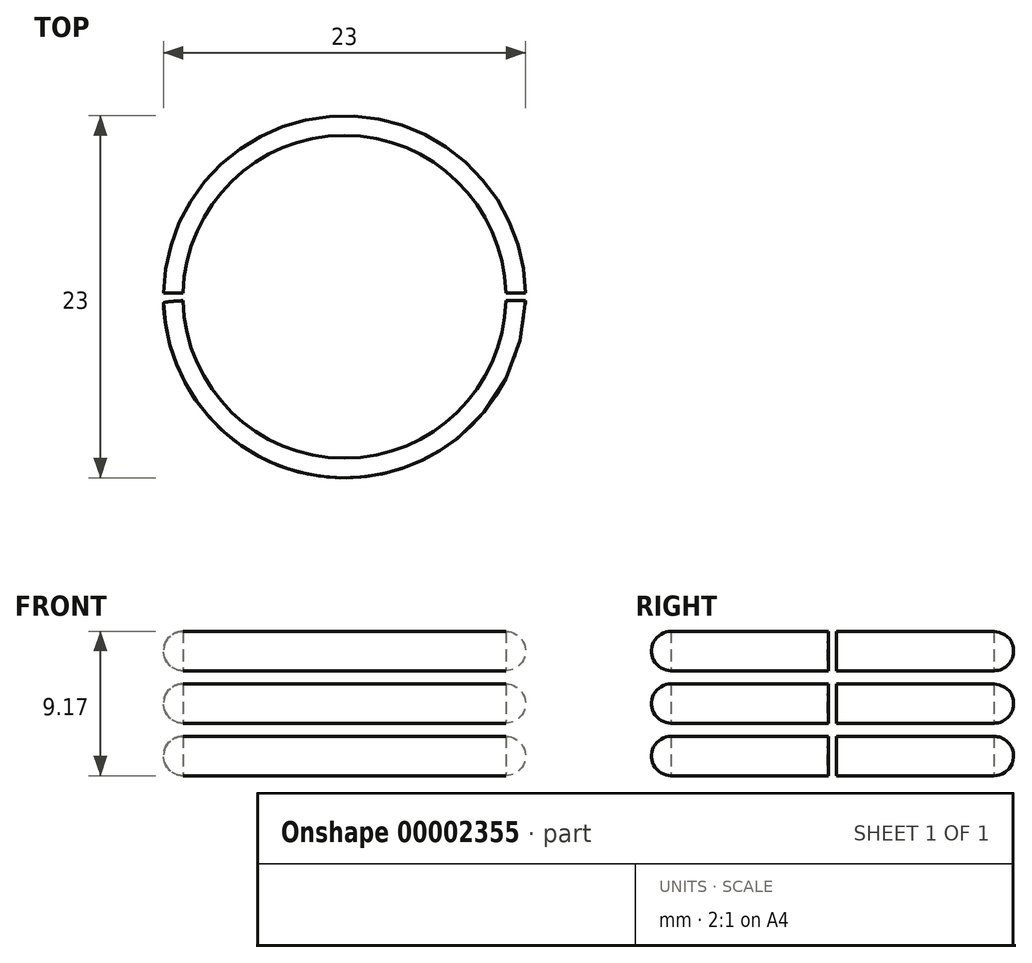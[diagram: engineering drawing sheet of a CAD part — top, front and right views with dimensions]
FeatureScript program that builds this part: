
annotation { "Feature Type Name" : "Feature", "Feature Type Description" : "" }
export const myFeature = defineFeature(function(context is Context, id is Id, definition is map)
    precondition{}
    {
        {
            var Q0;
            Q0=qCreatedBy(makeId("Top.planeOp"),FACE);
            var sketch = newSketch(context, id + "F0", { "sketchPlane" : qUnion([Q0])});
            skCircle(sketch, "E0", {"center": v(0, 0) * mm, "radius": 17.5 * mm});
            skSolve(sketch);
        }
        {
            var Q0;
            Q0=qSketchRegion(id+"F0",true);
            extrude(context, id + "F1", {"entities" : qUnion([Q0]), "depth" : 6 * mm, "hasSecondDirection" : true, "secondDirectionOppositeDirection" : true, "secondDirectionDepth" : 9 * mm});
        }
        {
            var Q0;
            Q0=makeQuery(id+"F1.opExtrude","CAP_FACE",FACE,{"disambiguationData":[OSD([sQuery(id+"F0.wireOp",EDGE,"E0")])],"isStart":false});
            var sketch = newSketch(context, id + "F2", { "sketchPlane" : qUnion([Q0])});
            skCircle(sketch, "E1", {"center": v(0, 0) * mm, "radius": 10.25 * mm});
            skSolve(sketch);
        }
        {
            var Q0;
            Q0=qSketchRegion(id+"F2",true);
            extrude(context, id + "F3", {"entities" : qUnion([Q0]), "operationType" : NewBodyOperationType.ADD, "depth" : 10 * mm});
        }
        {
            var Q0;
            Q0=qCreatedBy(makeId("Top.planeOp"),FACE);
            var sketch = newSketch(context, id + "F4", { "sketchPlane" : qUnion([Q0])});
            skLineSegment(sketch, "E2", {"start": v(0, 0) * mm, "end": v(0, 17.5) * mm, "construction": true});
            skLineSegment(sketch, "E3", {"start": v(0, 18.5) * mm, "end": v(2, 18.4) * mm});
            skLineSegment(sketch, "E4", {"start": v(2, 18.4) * mm, "end": v(1.89, 17.4) * mm});
            skArc(sketch, "E5.0", {"start": v(1.89, 17.4) * mm, "mid": v(0.95, 17.47) * mm, "end": v(0, 17.5) * mm});
            skLineSegment(sketch, "E6", {"start": v(0, 17.5) * mm, "end": v(0, 18.5) * mm});
            skLineSegment(sketch, "E7", {"start": v(1.89, 17.4) * mm, "end": v(0, 0) * mm, "construction": true});
            skSolve(sketch);
        }
        {
            var Q0;
            Q0=qSketchRegion(id+"F4",true);
            var Q1;
            Q1=makeQuery(id+"F1.opExtrude","CAP_FACE",FACE,{"disambiguationData":[OSD([sQuery(id+"F0.wireOp",EDGE,"E0")])],"isStart":false});
            var Q3;
            Q3=makeQuery(id+"F1.opExtrude","CAP_FACE",FACE,{"disambiguationData":[OSD([sQuery(id+"F0.wireOp",EDGE,"E0")])],"isStart":true});
            extrude(context, id + "F5", {"entities" : qUnion([Q0]), "operationType" : NewBodyOperationType.ADD, "endBound" : BoundingType.UP_TO_SURFACE, "endBoundEntityFace" : qUnion([Q1]), "depth" : 6 * mm, "hasSecondDirection" : true, "secondDirectionBound" : SecondDirectionBoundingType.UP_TO_SURFACE, "secondDirectionOppositeDirection" : true, "secondDirectionBoundEntityFace" : qUnion([Q3]), "secondDirectionDepth" : 9 * mm});
        }
        {
            var Q0;
            Q0=makeQuery(id+"F5.opExtrude","SWEPT_FACE",FACE,{"disambiguationData":[OSD([sQuery(id+"F4.wireOp",EDGE,"E3")])]});
            var Q1;
            Q1=makeQuery(id+"F5.opExtrude","SWEPT_FACE",FACE,{"disambiguationData":[OSD([sQuery(id+"F4.wireOp",EDGE,"E4")])]});
            var Q2;
            Q2=makeQuery(id+"F5.opExtrude","SWEPT_FACE",FACE,{"disambiguationData":[OSD([sQuery(id+"F4.wireOp",EDGE,"E6")])]});
            var Q3;
            Q3=makeQuery(id+"F1.opExtrude","CAP_EDGE",EDGE,{"disambiguationData":[OSD([sQuery(id+"F0.wireOp",EDGE,"E0")])],"isStart":false});
            circularPattern(context, id + "F6", {"faces" : qUnion([Q0, Q1, Q2]), "axis" : qUnion([Q3]), "angle" : 360 * degree, "instanceCount" : 30, "equalSpace" : true, "patternType" : PatternType.FACE});
        }
        {
            var Q0;
            Q0=qCreatedBy(makeId("Front.planeOp"),FACE);
            var sketch = newSketch(context, id + "F7", { "sketchPlane" : qUnion([Q0])});
            skArc(sketch, "E8", {"start": v(-10.25, 16) * mm, "mid": v(-11.5, 14.75) * mm, "end": v(-10.25, 13.5) * mm});
            skArc(sketch, "E9", {"start": v(-10.25, 12.67) * mm, "mid": v(-11.5, 11.42) * mm, "end": v(-10.25, 10.17) * mm});
            skLineSegment(sketch, "E10", {"start": v(-10.25, 16) * mm, "end": v(-10.25, 13.5) * mm});
            skArc(sketch, "E11", {"start": v(-10.25, 9.33) * mm, "mid": v(-11.5, 8.08) * mm, "end": v(-10.25, 6.83) * mm});
            skLineSegment(sketch, "E12", {"start": v(-10.25, 13.5) * mm, "end": v(-10.25, 12.67) * mm, "construction": true});
            skLineSegment(sketch, "E13", {"start": v(-10.25, 12.67) * mm, "end": v(-10.25, 10.17) * mm});
            skLineSegment(sketch, "E14", {"start": v(-10.25, 10.17) * mm, "end": v(-10.25, 9.33) * mm, "construction": true});
            skLineSegment(sketch, "E15", {"start": v(-10.25, 9.33) * mm, "end": v(-10.25, 6.83) * mm});
            skLineSegment(sketch, "E16", {"start": v(-10.25, 6.83) * mm, "end": v(-10.25, 6) * mm, "construction": true});
            skSolve(sketch);
        }
        {
            var Q0;
            Q0=makeQuery(id+"F7.imprint","IMPRINT",FACE,{"disambiguationData":[TD([[makeQuery(id+"F7.imprint","IMPRINT",EDGE,{"derivedFrom":sQuery(id+"F7.wireOp",EDGE,"E8")}),1.0]])]});
            var Q1;
            Q1=makeQuery(id+"F7.imprint","IMPRINT",FACE,{"disambiguationData":[TD([[makeQuery(id+"F7.imprint","IMPRINT",EDGE,{"derivedFrom":sQuery(id+"F7.wireOp",EDGE,"E9")}),1.0]])]});
            var Q2;
            Q2=makeQuery(id+"F7.imprint","IMPRINT",FACE,{"disambiguationData":[TD([[makeQuery(id+"F7.imprint","IMPRINT",EDGE,{"derivedFrom":sQuery(id+"F7.wireOp",EDGE,"E11")}),1.0]])]});
            var Q3;
            Q3=sQuery(id+"F7.wireOp",EDGE,"E8");
            var Q4;
            Q4=sQuery(id+"F7.wireOp",EDGE,"E9");
            var Q5;
            Q5=sQuery(id+"F7.wireOp",EDGE,"E11");
            var Q6;
            Q6=makeQuery(id+"F3.opExtrude","CAP_EDGE",EDGE,{"disambiguationData":[OSD([sQuery(id+"F2.wireOp",EDGE,"E1")])],"isStart":false});
            revolve(context, id + "F8", {"entities" : qUnion([Q0, Q1, Q2]), "surfaceEntities" : qUnion([Q3, Q4, Q5]), "axis" : qUnion([Q6]), "revolveType" : RevolveType.FULL});
        }
        {
            var Q0;
            Q0=makeQuery(id+"F3.opExtrude","CAP_FACE",FACE,{"disambiguationData":[OSD([sQuery(id+"F2.wireOp",EDGE,"E1")])],"isStart":false});
            var sketch = newSketch(context, id + "F9", { "sketchPlane" : qUnion([Q0])});
            skCircle(sketch, "E17", {"center": v(0, 0) * mm, "radius": 8.25 * mm});
            skSolve(sketch);
        }
        {
            var Q0;
            Q0 = qSketchRegion(id + "F9", true);
            var Q1;
            Q1=makeQuery(id+"F5.boolean.opBoolean","MERGE",FACE,{"derivedFrom":[makeQuery(id+"F1.opExtrude","CAP_FACE",FACE,{"disambiguationData":[OSD([sQuery(id+"F0.wireOp",EDGE,"E0")])],"isStart":false}),makeQuery(id+"F5.opExtrude","CAP_FACE",FACE,{"disambiguationData":[OSD([sQuery(id+"F4.wireOp",EDGE,"E3"),sQuery(id+"F4.wireOp",EDGE,"E4"),sQuery(id+"F4.wireOp",EDGE,"E5.0"),sQuery(id+"F4.wireOp",EDGE,"E6")])],"isStart":false})]});
            extrude(context, id + "F10", {"entities" : qUnion([Q0]), "operationType" : NewBodyOperationType.REMOVE, "endBound" : BoundingType.UP_TO_SURFACE, "oppositeDirection" : true, "endBoundEntityFace" : qUnion([Q1]), "depth" : 25 * mm});
        }
        {
            var Q0;
            {var subQ0=sQuery(id+"F9.wireOp",EDGE,"E17");Q0=makeQuery(id+"F14.boolean.opBoolean","SPLIT",FACE,{"disambiguationData":[TD([makeQuery(id+"F14.opExtrude","SWEPT_FACE",FACE,{"disambiguationData":[OSD([sQuery(id+"F13.wireOp",EDGE,"E19.rect.bottom")])]})])],"derivedFrom":makeQuery(id+"F10.boolean.opBoolean","COPY",FACE,{"derivedFrom":makeQuery(id+"F10.opExtrude","CAP_FACE",FACE,{"disambiguationData":[OSD([subQ0])],"isStart":false})})});}
            var sketch = newSketch(context, id + "F11", { "sketchPlane" : qUnion([Q0])});
            skCircle(sketch, "E18", {"center": v(0, 0) * mm, "radius": 3 * mm});
            skSolve(sketch);
        }
        {
            var Q0;
            Q0 = qSketchRegion(id + "F11", true);
            extrude(context, id + "F12", {"entities" : qUnion([Q0]), "operationType" : NewBodyOperationType.REMOVE, "endBound" : BoundingType.THROUGH_ALL, "oppositeDirection" : true, "depth" : 25 * mm});
        }
        {
            var Q0;
            Q0=makeQuery(id+"F9.imprint","IMPRINT",FACE,{"disambiguationData":[TD([[makeQuery(id+"F9.imprint","IMPRINT",EDGE,{"derivedFrom":sQuery(id+"F9.wireOp",EDGE,"E17")}),-1.0]])]});
            var sketch = newSketch(context, id + "F13", { "sketchPlane" : qUnion([Q0])});
            skLineSegment(sketch, "E19.rect.bottom", {"start": v(20, 0.25) * mm, "end": v(-20, 0.25) * mm});
            skLineSegment(sketch, "E19.rect.top", {"start": v(20, -0.25) * mm, "end": v(-20, -0.25) * mm});
            skLineSegment(sketch, "E19.rect.left", {"start": v(20, 0.25) * mm, "end": v(20, -0.25) * mm});
            skLineSegment(sketch, "E19.rect.right", {"start": v(-20, 0.25) * mm, "end": v(-20, -0.25) * mm});
            skPoint(sketch, "E19.rect.middle", {"position": v(0, 0) * mm});
            skSolve(sketch);
        }
        {
            var Q0;
            Q0 = qSketchRegion(id + "F13", true);
            extrude(context, id + "F14", {"entities" : qUnion([Q0]), "operationType" : NewBodyOperationType.REMOVE, "endBound" : BoundingType.THROUGH_ALL, "oppositeDirection" : true, "depth" : 25 * mm});
        }
        {
            var Q0;
            Q0=makeQuery(id+"F14.boolean.opBoolean","COPY",FACE,{"disambiguationData":[OD(0.0)],"derivedFrom":makeQuery(id+"F14.opExtrude","SWEPT_FACE",FACE,{"disambiguationData":[OSD([sQuery(id+"F13.wireOp",EDGE,"E19.rect.top")])]})});
            var sketch = newSketch(context, id + "F15", { "sketchPlane" : qUnion([Q0])});
            skLineSegment(sketch, "E20.bottom", {"start": v(18.48, -5) * mm, "end": v(4.99, -5) * mm});
            skLineSegment(sketch, "E20.top", {"start": v(18.48, 2) * mm, "end": v(4.99, 2) * mm});
            skLineSegment(sketch, "E20.left", {"start": v(18.48, -5) * mm, "end": v(18.48, 2) * mm});
            skLineSegment(sketch, "E20.right", {"start": v(4.99, -5) * mm, "end": v(4.99, 2) * mm});
            skLineSegment(sketch, "E21", {"start": v(6.7, 2) * mm, "end": v(6.7, 6) * mm, "construction": true});
            skLineSegment(sketch, "E22", {"start": v(6.7, -5) * mm, "end": v(6.7, -9) * mm, "construction": true});
            skSolve(sketch);
        }
        {
            var Q0;
            Q0 = qSketchRegion(id + "F15", true);
            var Q1;
            Q1=sQuery(id+"F15.wireOp",EDGE,"E20.left");
            revolve(context, id + "F16", {"operationType" : NewBodyOperationType.REMOVE, "entities" : qUnion([Q0]), "axis" : qUnion([Q1]), "revolveType" : RevolveType.ONE_DIRECTION, "oppositeDirection" : true, "angle" : 90 * degree});
        }
        {
            var Q0;
            Q0=makeQuery(id+"F14.boolean.opBoolean","COPY",FACE,{"disambiguationData":[OD(0.0)],"derivedFrom":makeQuery(id+"F14.opExtrude","SWEPT_FACE",FACE,{"disambiguationData":[OSD([sQuery(id+"F13.wireOp",EDGE,"E19.rect.bottom")])]})});
            var sketch = newSketch(context, id + "F17", { "sketchPlane" : qUnion([Q0])});
            skLineSegment(sketch, "E23.bottom", {"start": v(-17.5, -4.5) * mm, "end": v(-6.5, -4.5) * mm});
            skLineSegment(sketch, "E23.top", {"start": v(-17.5, 1.5) * mm, "end": v(-6.5, 1.5) * mm});
            skLineSegment(sketch, "E23.left", {"start": v(-17.5, 1.5) * mm, "end": v(-17.5, -4.5) * mm});
            skLineSegment(sketch, "E23.right", {"start": v(-6.5, 1.5) * mm, "end": v(-6.5, -4.5) * mm});
            skLineSegment(sketch, "E24", {"start": v(-6.5, 1.5) * mm, "end": v(-6.5, 6) * mm, "construction": true});
            skLineSegment(sketch, "E25", {"start": v(-6.5, -4.5) * mm, "end": v(-6.5, -9) * mm, "construction": true});
            skSolve(sketch);
        }
        {
            var Q0;
            Q0 = qSketchRegion(id + "F17", true);
            var Q1;
            Q1=sQuery(id+"F17.wireOp",EDGE,"E23.left");
            revolve(context, id + "F18", {"operationType" : NewBodyOperationType.ADD, "entities" : qUnion([Q0]), "axis" : qUnion([Q1]), "revolveType" : RevolveType.ONE_DIRECTION, "angle" : 65 * degree});
        }
        {
            var Q0;
            {var subQ0=sQuery(id+"F0.wireOp",EDGE,"E0");var subQ1=sQuery(id+"F4.wireOp",EDGE,"E3");var subQ2=sQuery(id+"F4.wireOp",EDGE,"E4");var subQ3=sQuery(id+"F4.wireOp",EDGE,"E6");var subQ6=makeQuery(id+"F5.opExtrude","SWEPT_FACE",FACE,{"disambiguationData":[OSD([subQ1])]});Q0=makeQuery(id+"F14.boolean.opBoolean","SPLIT",FACE,{"disambiguationData":[TD([subQ6])],"derivedFrom":makeQuery(id+"F5.boolean.opBoolean","MERGE",FACE,{"derivedFrom":[makeQuery(id+"F1.opExtrude","CAP_FACE",FACE,{"disambiguationData":[OSD([subQ0])],"isStart":false}),makeQuery(id+"F5.opExtrude","CAP_FACE",FACE,{"disambiguationData":[OSD([subQ1,subQ2,sQuery(id+"F4.wireOp",EDGE,"E5.0"),subQ3])],"isStart":false})]})});}
            var Q1;
            {var subQ0=sQuery(id+"F0.wireOp",EDGE,"E0");var subQ1=sQuery(id+"F4.wireOp",EDGE,"E3");var subQ2=sQuery(id+"F4.wireOp",EDGE,"E4");var subQ3=sQuery(id+"F4.wireOp",EDGE,"E6");var subQ6=makeQuery(id+"F5.opExtrude","SWEPT_FACE",FACE,{"disambiguationData":[OSD([subQ1])]});Q1=makeQuery(id+"F14.boolean.opBoolean","SPLIT",FACE,{"disambiguationData":[TD([subQ6])],"derivedFrom":makeQuery(id+"F5.boolean.opBoolean","MERGE",FACE,{"derivedFrom":[makeQuery(id+"F1.opExtrude","CAP_FACE",FACE,{"disambiguationData":[OSD([subQ0])],"isStart":true}),makeQuery(id+"F5.opExtrude","CAP_FACE",FACE,{"disambiguationData":[OSD([subQ1,subQ2,sQuery(id+"F4.wireOp",EDGE,"E5.0"),subQ3])],"isStart":true})]})});}
            cPlane(context, id + "F19", {"entities" : qUnion([Q0, Q1]), "cplaneType" : CPlaneType.MID_PLANE, "offset" : 2.5 * mm, "oppositeDirection" : true, "width" : 150 * mm, "height" : 150 * mm});
        }
        {
            var Q0;
            Q0=qCreatedBy(id+"F19.planeOp",FACE);
            var sketch = newSketch(context, id + "F20", { "sketchPlane" : qUnion([Q0])});
            skCircle(sketch, "E26", {"center": v(-11.8, -6.06) * mm, "radius": 2.5 * mm});
            skSolve(sketch);
        }
        {
            var Q0;
            Q0 = qSketchRegion(id + "F20", true);
            var Q1;
            {var subQ0=sQuery(id+"F0.wireOp",EDGE,"E0");var subQ1=sQuery(id+"F4.wireOp",EDGE,"E3");var subQ2=sQuery(id+"F4.wireOp",EDGE,"E4");var subQ3=sQuery(id+"F4.wireOp",EDGE,"E6");var subQ6=makeQuery(id+"F5.opExtrude","SWEPT_FACE",FACE,{"disambiguationData":[OSD([subQ1])]});Q1=makeQuery(id+"F14.boolean.opBoolean","SPLIT",FACE,{"disambiguationData":[TD([makeQuery(id+"F6.opPattern","COPY",FACE,{"derivedFrom":subQ6,"instanceName":"8"})])],"derivedFrom":makeQuery(id+"F5.boolean.opBoolean","MERGE",FACE,{"derivedFrom":[makeQuery(id+"F1.opExtrude","CAP_FACE",FACE,{"disambiguationData":[OSD([subQ0])],"isStart":false}),makeQuery(id+"F5.opExtrude","CAP_FACE",FACE,{"disambiguationData":[OSD([subQ1,subQ2,sQuery(id+"F4.wireOp",EDGE,"E5.0"),subQ3])],"isStart":false})]})});}
            var Q2;
            {var subQ0=sQuery(id+"F0.wireOp",EDGE,"E0");var subQ1=sQuery(id+"F4.wireOp",EDGE,"E3");var subQ2=sQuery(id+"F4.wireOp",EDGE,"E4");var subQ3=sQuery(id+"F4.wireOp",EDGE,"E6");var subQ6=makeQuery(id+"F5.opExtrude","SWEPT_FACE",FACE,{"disambiguationData":[OSD([subQ1])]});Q2=makeQuery(id+"F14.boolean.opBoolean","SPLIT",FACE,{"disambiguationData":[TD([makeQuery(id+"F6.opPattern","COPY",FACE,{"derivedFrom":subQ6,"instanceName":"8"})])],"derivedFrom":makeQuery(id+"F5.boolean.opBoolean","MERGE",FACE,{"derivedFrom":[makeQuery(id+"F1.opExtrude","CAP_FACE",FACE,{"disambiguationData":[OSD([subQ0])],"isStart":true}),makeQuery(id+"F5.opExtrude","CAP_FACE",FACE,{"disambiguationData":[OSD([subQ1,subQ2,sQuery(id+"F4.wireOp",EDGE,"E5.0"),subQ3])],"isStart":true})]})});}
            extrude(context, id + "F21", {"entities" : qUnion([Q0]), "operationType" : NewBodyOperationType.ADD, "endBound" : BoundingType.UP_TO_SURFACE, "endBoundEntityFace" : qUnion([Q1]), "depth" : 15 * mm, "hasSecondDirection" : true, "secondDirectionBound" : SecondDirectionBoundingType.UP_TO_SURFACE, "secondDirectionOppositeDirection" : true, "secondDirectionBoundEntityFace" : qUnion([Q2]), "secondDirectionDepth" : 25 * mm});
        }
        {
            var Q0;
            {var subQ0=sQuery(id+"F17.wireOp",EDGE,"E23.top");var subQ1=makeQuery(id+"F18.opRevolve","SWEPT_FACE",FACE,{"disambiguationData":[OSD([subQ0])]});var subQ2=sQuery(id+"F17.wireOp",EDGE,"E23.right");Q0=makeQuery(id+"F21.boolean.opBoolean","SPLIT",FACE,{"disambiguationData":[TD([makeQuery(id+"F1.opExtrude","SWEPT_FACE",FACE,{"disambiguationData":[OSD([sQuery(id+"F0.wireOp",EDGE,"E0")])]}),makeQuery(id+"F14.boolean.opBoolean","COPY",FACE,{"disambiguationData":[OD(1.0)],"derivedFrom":makeQuery(id+"F14.opExtrude","SWEPT_FACE",FACE,{"disambiguationData":[OSD([sQuery(id+"F13.wireOp",EDGE,"E19.rect.bottom")])]})}),makeQuery(id+"F18.opRevolve","CAP_FACE",FACE,{"disambiguationData":[OSD([sQuery(id+"F17.wireOp",EDGE,"E23.bottom"),subQ0,sQuery(id+"F17.wireOp",EDGE,"E23.left"),subQ2])],"isStart":false}),subQ1,makeQuery(id+"F18.opRevolve","SWEPT_FACE",FACE,{"disambiguationData":[OSD([subQ2])]}),makeQuery(id+"F21.opExtrude","SWEPT_FACE",FACE,{"disambiguationData":[OSD([sQuery(id+"F20.wireOp",EDGE,"E26")])]})])],"derivedFrom":subQ1});}
            var sketch = newSketch(context, id + "F22", { "sketchPlane" : qUnion([Q0])});
            skCircle(sketch, "E27.0", {"center": v(-11.8, -6.06) * mm, "radius": 2.5 * mm});
            skCircle(sketch, "E28", {"center": v(-11.8, -6.06) * mm, "radius": 3 * mm});
            skSolve(sketch);
        }
        {
            var Q0;
            Q0 = qSketchRegion(id + "F22", true);
            var Q1;
            {var subQ0=sQuery(id+"F0.wireOp",EDGE,"E0");var subQ1=sQuery(id+"F4.wireOp",EDGE,"E3");var subQ2=sQuery(id+"F4.wireOp",EDGE,"E4");var subQ3=sQuery(id+"F4.wireOp",EDGE,"E6");var subQ6=makeQuery(id+"F5.opExtrude","SWEPT_FACE",FACE,{"disambiguationData":[OSD([subQ1])]});Q1=makeQuery(id+"F14.boolean.opBoolean","SPLIT",FACE,{"disambiguationData":[TD([subQ6])],"derivedFrom":makeQuery(id+"F5.boolean.opBoolean","MERGE",FACE,{"derivedFrom":[makeQuery(id+"F1.opExtrude","CAP_FACE",FACE,{"disambiguationData":[OSD([subQ0])],"isStart":false}),makeQuery(id+"F5.opExtrude","CAP_FACE",FACE,{"disambiguationData":[OSD([subQ1,subQ2,sQuery(id+"F4.wireOp",EDGE,"E5.0"),subQ3])],"isStart":false})]})});}
            extrude(context, id + "F23", {"entities" : qUnion([Q0]), "operationType" : NewBodyOperationType.REMOVE, "endBound" : BoundingType.UP_TO_SURFACE, "endBoundEntityFace" : qUnion([Q1]), "depth" : 25 * mm});
        }
        {
            var Q0;
            {var subQ0=sQuery(id+"F17.wireOp",EDGE,"E23.bottom");var subQ1=makeQuery(id+"F18.opRevolve","SWEPT_FACE",FACE,{"disambiguationData":[OSD([subQ0])]});var subQ2=sQuery(id+"F17.wireOp",EDGE,"E23.right");Q0=makeQuery(id+"F21.boolean.opBoolean","SPLIT",FACE,{"disambiguationData":[TD([makeQuery(id+"F1.opExtrude","SWEPT_FACE",FACE,{"disambiguationData":[OSD([sQuery(id+"F0.wireOp",EDGE,"E0")])]}),makeQuery(id+"F14.boolean.opBoolean","COPY",FACE,{"disambiguationData":[OD(1.0)],"derivedFrom":makeQuery(id+"F14.opExtrude","SWEPT_FACE",FACE,{"disambiguationData":[OSD([sQuery(id+"F13.wireOp",EDGE,"E19.rect.bottom")])]})}),subQ1,makeQuery(id+"F18.opRevolve","CAP_FACE",FACE,{"disambiguationData":[OSD([subQ0,sQuery(id+"F17.wireOp",EDGE,"E23.top"),sQuery(id+"F17.wireOp",EDGE,"E23.left"),subQ2])],"isStart":false}),makeQuery(id+"F18.opRevolve","SWEPT_FACE",FACE,{"disambiguationData":[OSD([subQ2])]}),makeQuery(id+"F21.opExtrude","SWEPT_FACE",FACE,{"disambiguationData":[OSD([sQuery(id+"F20.wireOp",EDGE,"E26")])]})])],"derivedFrom":subQ1});}
            var sketch = newSketch(context, id + "F24", { "sketchPlane" : qUnion([Q0])});
            skCircle(sketch, "E29.0", {"center": v(-11.8, 6.06) * mm, "radius": 2.5 * mm});
            skCircle(sketch, "E30", {"center": v(-11.8, 6.06) * mm, "radius": 3 * mm});
            skSolve(sketch);
        }
        {
            var Q0;
            Q0 = qSketchRegion(id + "F24", true);
            var Q1;
            {var subQ0=sQuery(id+"F0.wireOp",EDGE,"E0");var subQ1=sQuery(id+"F4.wireOp",EDGE,"E3");var subQ2=sQuery(id+"F4.wireOp",EDGE,"E4");var subQ3=sQuery(id+"F4.wireOp",EDGE,"E6");var subQ6=makeQuery(id+"F5.opExtrude","SWEPT_FACE",FACE,{"disambiguationData":[OSD([subQ1])]});Q1=makeQuery(id+"F14.boolean.opBoolean","SPLIT",FACE,{"disambiguationData":[TD([makeQuery(id+"F6.opPattern","COPY",FACE,{"derivedFrom":subQ6,"instanceName":"8"})])],"derivedFrom":makeQuery(id+"F5.boolean.opBoolean","MERGE",FACE,{"derivedFrom":[makeQuery(id+"F1.opExtrude","CAP_FACE",FACE,{"disambiguationData":[OSD([subQ0])],"isStart":true}),makeQuery(id+"F5.opExtrude","CAP_FACE",FACE,{"disambiguationData":[OSD([subQ1,subQ2,sQuery(id+"F4.wireOp",EDGE,"E5.0"),subQ3])],"isStart":true})]})});}
            extrude(context, id + "F25", {"entities" : qUnion([Q0]), "operationType" : NewBodyOperationType.REMOVE, "endBound" : BoundingType.UP_TO_SURFACE, "endBoundEntityFace" : qUnion([Q1]), "depth" : 25 * mm});
        }
        {
            var Q0;
            Q0=qCreatedBy(id+"F19.planeOp",FACE);
            var sketch = newSketch(context, id + "F26", { "sketchPlane" : qUnion([Q0])});
            skArc(sketch, "E31", {"start": v(-10.25, -0.25) * mm, "mid": v(-14.36, -1.7) * mm, "end": v(-16.64, -5.4) * mm});
            skLineSegment(sketch, "E32", {"start": v(-10.25, -0.25) * mm, "end": v(-31.15, -0.25) * mm});
            skLineSegment(sketch, "E33", {"start": v(-31.15, -0.25) * mm, "end": v(-21.19, -10.77) * mm});
            skLineSegment(sketch, "E34", {"start": v(-16.64, -5.4) * mm, "end": v(-21.19, -10.77) * mm});
            skSolve(sketch);
        }
        {
            var Q0;
            Q0 = qSketchRegion(id + "F26", true);
            extrude(context, id + "F27", {"entities" : qUnion([Q0]), "operationType" : NewBodyOperationType.REMOVE, "endBound" : BoundingType.THROUGH_ALL, "depth" : 25 * mm, "hasSecondDirection" : true, "secondDirectionBound" : SecondDirectionBoundingType.THROUGH_ALL, "secondDirectionOppositeDirection" : true, "secondDirectionDepth" : 25 * mm});
        }
        {
            var Q0;
            Q0=makeQuery(id+"F18.opRevolve","SWEPT_FACE",FACE,{"disambiguationData":[OSD([sQuery(id+"F17.wireOp",EDGE,"E23.top")])]});
            var sketch = newSketch(context, id + "F28", { "sketchPlane" : qUnion([Q0])});
            skArc(sketch, "E35.0", {"start": v(-10.12, -7.91) * mm, "mid": v(-12.3, -8.5) * mm, "end": v(-14.06, -7.11) * mm});
            skArc(sketch, "E36.0", {"start": v(-12.85, -9.72) * mm, "mid": v(-11.42, -8.92) * mm, "end": v(-10.12, -7.91) * mm});
            skLineSegment(sketch, "E37.0", {"start": v(-14.06, -7.11) * mm, "end": v(-12.85, -9.72) * mm});
            skSolve(sketch);
        }
        {
            var Q0;
            Q0 = qSketchRegion(id + "F28", true);
            extrude(context, id + "F29", {"entities" : qUnion([Q0]), "operationType" : NewBodyOperationType.REMOVE, "endBound" : BoundingType.THROUGH_ALL, "oppositeDirection" : true, "depth" : 25 * mm});
        }
        {
            var Q0;
            Q0=makeQuery(id+"F23.boolean.opBoolean","SPLIT",BODY,{"disambiguationData":[OD(1.0)],"derivedFrom":makeQuery(id+"F14.boolean.opBoolean","SPLIT",BODY,{"disambiguationData":[OD(1.0)],"derivedFrom":makeQuery(id+"F1.opExtrude","SWEPT_BODY",BODY,{"disambiguationData":[OSD([sQuery(id+"F0.wireOp",EDGE,"E0")])]})})});
            var Q1;
            Q1=makeQuery(id+"F25.boolean.opBoolean","SPLIT",BODY,{"disambiguationData":[OD(1.0)],"derivedFrom":makeQuery(id+"F23.boolean.opBoolean","SPLIT",BODY,{"disambiguationData":[OD(0.0)],"derivedFrom":makeQuery(id+"F14.boolean.opBoolean","SPLIT",BODY,{"disambiguationData":[OD(1.0)],"derivedFrom":makeQuery(id+"F1.opExtrude","SWEPT_BODY",BODY,{"disambiguationData":[OSD([sQuery(id+"F0.wireOp",EDGE,"E0")])]})})})});
            deleteBodies(context, id + "F30", {"entities" : qUnion([Q0, Q1])});
        }
    });
